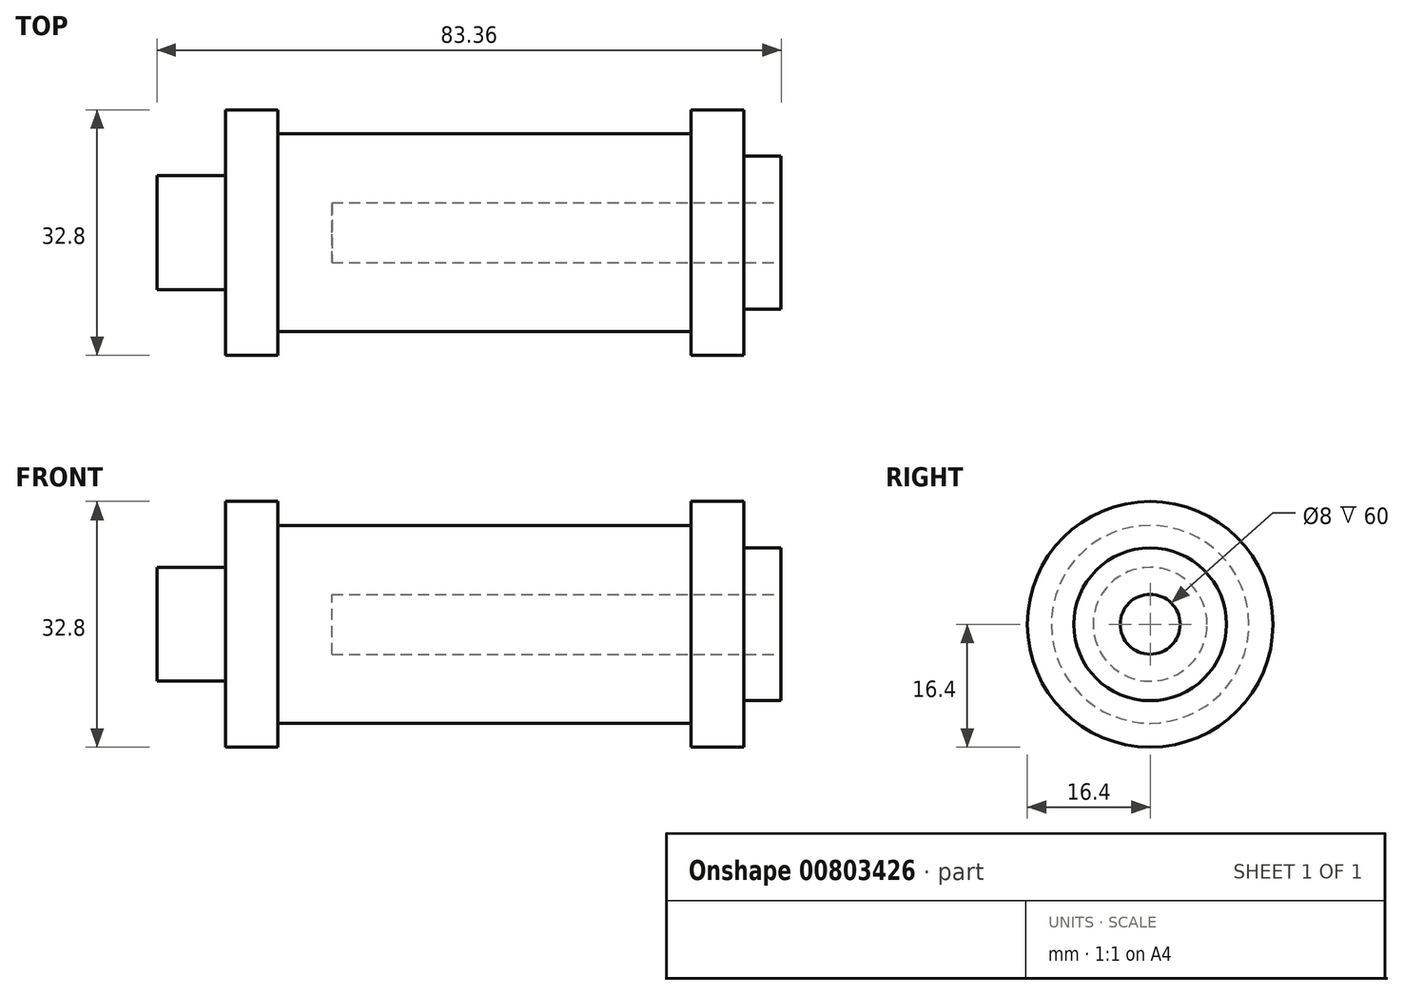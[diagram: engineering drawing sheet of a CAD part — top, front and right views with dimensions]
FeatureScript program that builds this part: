
annotation { "Feature Type Name" : "Feature", "Feature Type Description" : "" }
export const myFeature = defineFeature(function(context is Context, id is Id, definition is map)
    precondition{}
    {
        {
            var Q0;
            Q0=qCreatedBy(makeId("Top.planeOp"),FACE);
            var sketch = newSketch(context, id + "F0", { "sketchPlane" : qUnion([Q0])});
            skLineSegment(sketch, "E0", {"start": v(0, 0) * mm, "end": v(0, 7.6) * mm});
            skLineSegment(sketch, "E1", {"start": v(0, 7.6) * mm, "end": v(9.16, 7.6) * mm});
            skLineSegment(sketch, "E2", {"start": v(9.16, 7.6) * mm, "end": v(9.16, 16.4) * mm});
            skLineSegment(sketch, "E3", {"start": v(9.16, 16.4) * mm, "end": v(16.16, 16.4) * mm});
            skLineSegment(sketch, "E4", {"start": v(16.16, 16.4) * mm, "end": v(16.16, 13.2) * mm});
            skLineSegment(sketch, "E5", {"start": v(16.16, 13.2) * mm, "end": v(71.36, 13.2) * mm});
            skLineSegment(sketch, "E6", {"start": v(71.36, 13.2) * mm, "end": v(71.36, 16.4) * mm});
            skLineSegment(sketch, "E7", {"start": v(71.36, 16.4) * mm, "end": v(78.36, 16.4) * mm});
            skLineSegment(sketch, "E8", {"start": v(78.36, 16.4) * mm, "end": v(78.36, 10.2) * mm});
            skLineSegment(sketch, "E9", {"start": v(78.36, 10.2) * mm, "end": v(83.36, 10.2) * mm});
            skLineSegment(sketch, "E10", {"start": v(83.36, 10.2) * mm, "end": v(83.36, 0) * mm});
            skLineSegment(sketch, "E11", {"start": v(83.36, 0) * mm, "end": v(0, 0) * mm});
            skSolve(sketch);
        }
        {
            var Q0;
            Q0=makeQuery(id+"F0.imprint","IMPRINT",FACE,{"disambiguationData":[TD([[makeQuery(id+"F0.imprint","IMPRINT",EDGE,{"derivedFrom":sQuery(id+"F0.wireOp",EDGE,"E0")}),-1.0]])]});
            var Q1;
            Q1=sQuery(id+"F0.wireOp",EDGE,"E11");
            revolve(context, id + "F1", {"surfaceOperationType" : NewSurfaceOperationType.NEW, "entities" : qUnion([Q0]), "axis" : qUnion([Q1]), "revolveType" : RevolveType.FULL});
        }
        {
            var Q0;
            Q0=makeQuery(id+"F1.opRevolve","SWEPT_FACE",FACE,{"disambiguationData":[OSD([sQuery(id+"F0.wireOp",EDGE,"E10")])]});
            var sketch = newSketch(context, id + "F2", { "sketchPlane" : qUnion([Q0])});
            skCircle(sketch, "E12", {"center": v(0, 0) * mm, "radius": 4 * mm});
            skSolve(sketch);
        }
        {
            var Q0;
            Q0=makeQuery(id+"F2.imprint","IMPRINT",FACE,{"disambiguationData":[TD([[makeQuery(id+"F2.imprint","IMPRINT",EDGE,{"derivedFrom":sQuery(id+"F2.wireOp",EDGE,"E12")}),1.0]])]});
            var Q1;
            Q1=sQuery(id+"F2.wireOp",EDGE,"E12");
            extrude(context, id + "F3", {"entities" : qUnion([Q0]), "operationType" : NewBodyOperationType.REMOVE, "surfaceEntities" : qUnion([Q1]), "oppositeDirection" : true, "depth" : 60 * mm, "offsetDistance" : 25 * mm});
        }
    });
